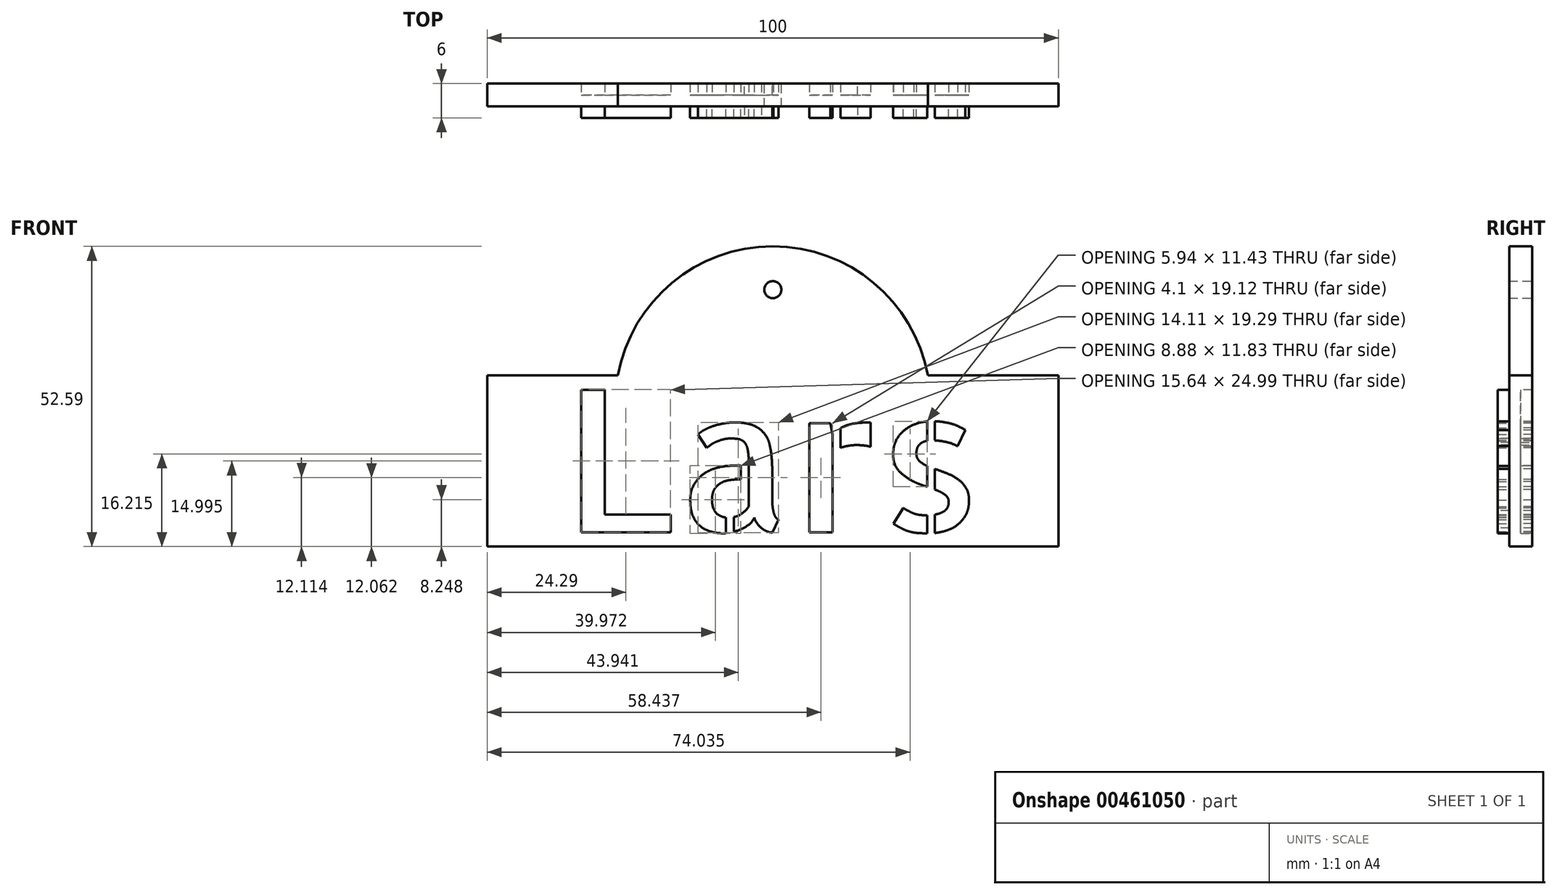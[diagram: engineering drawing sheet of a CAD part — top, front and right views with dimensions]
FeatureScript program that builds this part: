
annotation { "Feature Type Name" : "Feature", "Feature Type Description" : "" }
export const myFeature = defineFeature(function(context is Context, id is Id, definition is map)
    precondition{}
    {
        {
            var Q0;
            Q0=qCreatedBy(makeId("Front.planeOp"),FACE);
            var sketch = newSketch(context, id + "F0", { "sketchPlane" : qUnion([Q0])});
            skLineSegment(sketch, "E0.bottom", {"start": v(-240.63, 73.8) * mm, "end": v(-217.76, 73.8) * mm});
            skLineSegment(sketch, "E0.top", {"start": v(-240.63, 43.8) * mm, "end": v(-140.63, 43.8) * mm});
            skLineSegment(sketch, "E0.left", {"start": v(-240.63, 73.8) * mm, "end": v(-240.63, 43.8) * mm});
            skLineSegment(sketch, "E0.right", {"start": v(-140.63, 73.8) * mm, "end": v(-140.63, 43.8) * mm});
            skArc(sketch, "E1", {"start": v(-163.5, 73.8) * mm, "mid": v(-190.63, 96.4) * mm, "end": v(-217.76, 73.8) * mm});
            skPoint(sketch, "E2", {"position": v(-190.63, 43.8) * mm});
            skPoint(sketch, "E3", {"position": v(-190.63, 73.8) * mm});
            skPoint(sketch, "E4", {"position": v(-140.63, 58.8) * mm});
            skPoint(sketch, "E5", {"position": v(-240.63, 58.8) * mm});
            skCircle(sketch, "E6", {"center": v(-190.63, 88.8) * mm, "radius": 1.5 * mm});
            skText(sketch, "E7", { "text": "Lars\n", "fontName": "AllertaStencil-Regular.ttf"});
            skPoint(sketch, "E8", {"position": v(-227.31, 58.8) * mm});
            skLineSegment(sketch, "E9.trimOffspring", {"start": v(-163.5, 73.8) * mm, "end": v(-140.63, 73.8) * mm});
            const initialGuessF0  = {"E7": [-0.22731, 0.0463, 1, 0, 0.025]};
            skSetInitialGuess(sketch, initialGuessF0);
            skSolve(sketch);
        }
        {
            var Q0;
            Q0=makeQuery(id+"F0.imprint","IMPRINT",FACE,{"disambiguationData":[TD([[makeQuery(id+"F0.imprint","IMPRINT",EDGE,{"derivedFrom":sQuery(id+"F0.wireOp",EDGE,"E7.sketch_text.stroke-0")}),-1.0]])]});
            var Q1;
            Q1 = qSketchRegion(id + "F0", true);
            var Q2;
            Q2=makeQuery(id+"F0.imprint","IMPRINT",FACE,{"disambiguationData":[TD([[makeQuery(id+"F0.imprint","IMPRINT",EDGE,{"derivedFrom":sQuery(id+"F0.wireOp",EDGE,"E7.sketch_text.stroke-6")}),-1.0]])]});
            var Q3;
            Q3=makeQuery(id+"F0.imprint","IMPRINT",FACE,{"disambiguationData":[TD([[makeQuery(id+"F0.imprint","IMPRINT",EDGE,{"derivedFrom":sQuery(id+"F0.wireOp",EDGE,"E7.sketch_text.stroke-25")}),-1.0]])]});
            var Q4;
            Q4=makeQuery(id+"F0.imprint","IMPRINT",FACE,{"disambiguationData":[TD([[makeQuery(id+"F0.imprint","IMPRINT",EDGE,{"derivedFrom":sQuery(id+"F0.wireOp",EDGE,"E7.sketch_text.stroke-61")}),-1.0]])]});
            var Q5;
            Q5=makeQuery(id+"F0.imprint","IMPRINT",FACE,{"disambiguationData":[TD([[makeQuery(id+"F0.imprint","IMPRINT",EDGE,{"derivedFrom":sQuery(id+"F0.wireOp",EDGE,"E7.sketch_text.stroke-68")}),-1.0]])]});
            var Q6;
            Q6=makeQuery(id+"F0.imprint","IMPRINT",FACE,{"disambiguationData":[TD([[makeQuery(id+"F0.imprint","IMPRINT",EDGE,{"derivedFrom":sQuery(id+"F0.wireOp",EDGE,"E7.sketch_text.stroke-75")}),-1.0]])]});
            var Q7;
            Q7=makeQuery(id+"F0.imprint","IMPRINT",FACE,{"disambiguationData":[TD([[makeQuery(id+"F0.imprint","IMPRINT",EDGE,{"derivedFrom":sQuery(id+"F0.wireOp",EDGE,"E7.sketch_text.stroke-89")}),-1.0]])]});
            var Q8;
            Q8=makeQuery(id+"F0.imprint","IMPRINT",FACE,{"disambiguationData":[TD([[makeQuery(id+"F0.imprint","IMPRINT",EDGE,{"derivedFrom":sQuery(id+"F0.wireOp",EDGE,"E7.sketch_text.stroke-95")}),-1.0]])]});
            var Q9;
            Q9=makeQuery(id+"F0.imprint","IMPRINT",FACE,{"disambiguationData":[TD([[makeQuery(id+"F0.imprint","IMPRINT",EDGE,{"derivedFrom":sQuery(id+"F0.wireOp",EDGE,"E7.sketch_text.stroke-104")}),-1.0]])]});
            var Q10;
            Q10=makeQuery(id+"F0.imprint","IMPRINT",FACE,{"disambiguationData":[TD([[makeQuery(id+"F0.imprint","IMPRINT",EDGE,{"derivedFrom":sQuery(id+"F0.wireOp",EDGE,"E0.bottom")}),-1.0]])]});
            extrude(context, id + "F1", {"entities" : qUnion([Q0, Q1, Q2, Q3, Q4, Q5, Q6, Q7, Q8, Q9, Q10]), "depth" : 2 * mm, "offsetDistance" : 25 * mm});
        }
        {
            var Q0;
            Q0=makeQuery(id+"F0.imprint","IMPRINT",FACE,{"disambiguationData":[TD([[makeQuery(id+"F0.imprint","IMPRINT",EDGE,{"derivedFrom":sQuery(id+"F0.wireOp",EDGE,"E7.sketch_text.stroke-0")}),-1.0]])]});
            var Q1;
            Q1=makeQuery(id+"F0.imprint","IMPRINT",FACE,{"disambiguationData":[TD([[makeQuery(id+"F0.imprint","IMPRINT",EDGE,{"derivedFrom":sQuery(id+"F0.wireOp",EDGE,"E7.sketch_text.stroke-6")}),-1.0]])]});
            var Q2;
            Q2=makeQuery(id+"F0.imprint","IMPRINT",FACE,{"disambiguationData":[TD([[makeQuery(id+"F0.imprint","IMPRINT",EDGE,{"derivedFrom":sQuery(id+"F0.wireOp",EDGE,"E7.sketch_text.stroke-25")}),-1.0]])]});
            var Q3;
            Q3=makeQuery(id+"F0.imprint","IMPRINT",FACE,{"disambiguationData":[TD([[makeQuery(id+"F0.imprint","IMPRINT",EDGE,{"derivedFrom":sQuery(id+"F0.wireOp",EDGE,"E7.sketch_text.stroke-61")}),-1.0]])]});
            var Q4;
            Q4=makeQuery(id+"F0.imprint","IMPRINT",FACE,{"disambiguationData":[TD([[makeQuery(id+"F0.imprint","IMPRINT",EDGE,{"derivedFrom":sQuery(id+"F0.wireOp",EDGE,"E7.sketch_text.stroke-75")}),-1.0]])]});
            var Q5;
            Q5=makeQuery(id+"F0.imprint","IMPRINT",FACE,{"disambiguationData":[TD([[makeQuery(id+"F0.imprint","IMPRINT",EDGE,{"derivedFrom":sQuery(id+"F0.wireOp",EDGE,"E7.sketch_text.stroke-68")}),-1.0]])]});
            var Q6;
            Q6=makeQuery(id+"F0.imprint","IMPRINT",FACE,{"disambiguationData":[TD([[makeQuery(id+"F0.imprint","IMPRINT",EDGE,{"derivedFrom":sQuery(id+"F0.wireOp",EDGE,"E7.sketch_text.stroke-89")}),-1.0]])]});
            var Q7;
            Q7=makeQuery(id+"F0.imprint","IMPRINT",FACE,{"disambiguationData":[TD([[makeQuery(id+"F0.imprint","IMPRINT",EDGE,{"derivedFrom":sQuery(id+"F0.wireOp",EDGE,"E7.sketch_text.stroke-104")}),-1.0]])]});
            var Q8;
            Q8=makeQuery(id+"F0.imprint","IMPRINT",FACE,{"disambiguationData":[TD([[makeQuery(id+"F0.imprint","IMPRINT",EDGE,{"derivedFrom":sQuery(id+"F0.wireOp",EDGE,"E7.sketch_text.stroke-95")}),-1.0]])]});
            extrude(context, id + "F2", {"entities" : qUnion([Q0, Q1, Q2, Q3, Q4, Q5, Q6, Q7, Q8]), "operationType" : NewBodyOperationType.ADD, "depth" : 4 * mm, "offsetDistance" : 25 * mm});
        }
        {
            var Q0;
            Q0=makeQuery(id+"F0.imprint","IMPRINT",FACE,{"disambiguationData":[TD([[makeQuery(id+"F0.imprint","IMPRINT",EDGE,{"derivedFrom":sQuery(id+"F0.wireOp",EDGE,"E0.bottom")}),-1.0]])]});
            extrude(context, id + "F3", {"entities" : qUnion([Q0]), "operationType" : NewBodyOperationType.ADD, "oppositeDirection" : true, "depth" : 2 * mm, "offsetDistance" : 25 * mm});
        }
    });
